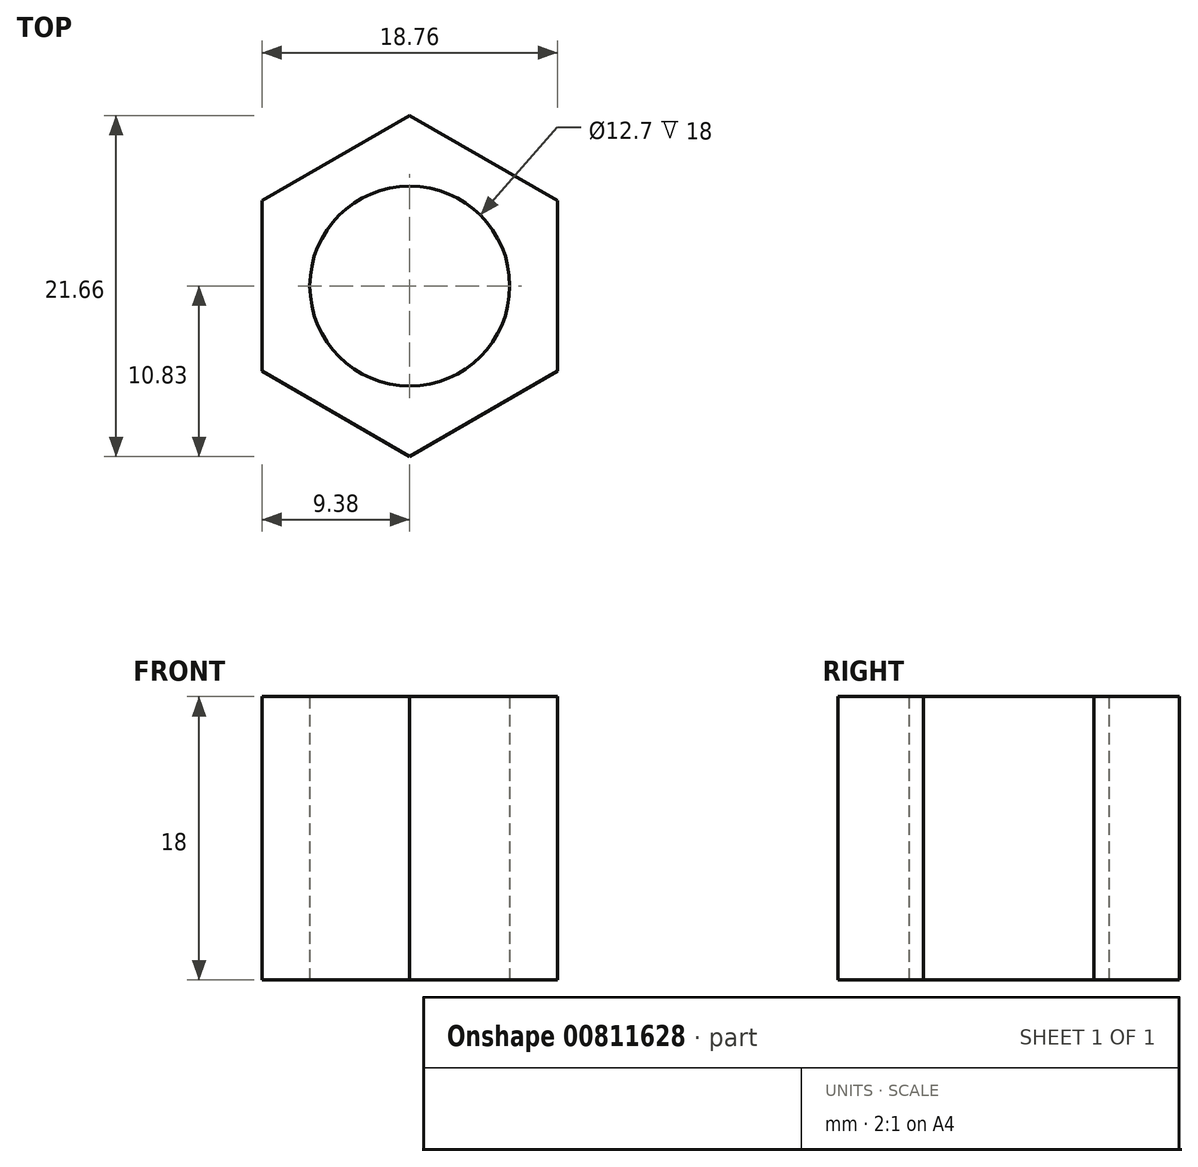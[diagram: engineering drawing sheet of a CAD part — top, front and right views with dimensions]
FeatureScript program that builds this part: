
annotation { "Feature Type Name" : "Feature", "Feature Type Description" : "" }
export const myFeature = defineFeature(function(context is Context, id is Id, definition is map)
    precondition{}
    {
        {
            var Q0;
            Q0=qCreatedBy(makeId("Top.planeOp"),FACE);
            var sketch = newSketch(context, id + "F0", { "sketchPlane" : qUnion([Q0])});
            skCircle(sketch, "E0.cCircle", {"center": v(0, 0) * mm, "radius": 9.38 * mm, "construction": true});
            skLineSegment(sketch, "E0.0", {"start": v(9.38, 5.42) * mm, "end": v(9.38, -5.42) * mm});
            skLineSegment(sketch, "E0.1", {"start": v(9.38, -5.42) * mm, "end": v(0, -10.83) * mm});
            skLineSegment(sketch, "E0.2", {"start": v(0, -10.83) * mm, "end": v(-9.38, -5.42) * mm});
            skLineSegment(sketch, "E0.3", {"start": v(-9.38, -5.42) * mm, "end": v(-9.38, 5.42) * mm});
            skLineSegment(sketch, "E0.4", {"start": v(-9.38, 5.42) * mm, "end": v(0, 10.83) * mm});
            skLineSegment(sketch, "E0.5", {"start": v(0, 10.83) * mm, "end": v(9.38, 5.42) * mm});
            skPoint(sketch, "E0.0.midPoint", {"position": v(9.38, 0) * mm});
            skCircle(sketch, "E1", {"center": v(0, 0) * mm, "radius": 6.35 * mm});
            skSolve(sketch);
        }
        {
            var Q0;
            Q0 = qSketchRegion(id + "F0", true);
            extrude(context, id + "F1", {"entities" : qUnion([Q0]), "depth" : 18 * mm, "offsetDistance" : 25.4 * mm});
        }
    });
